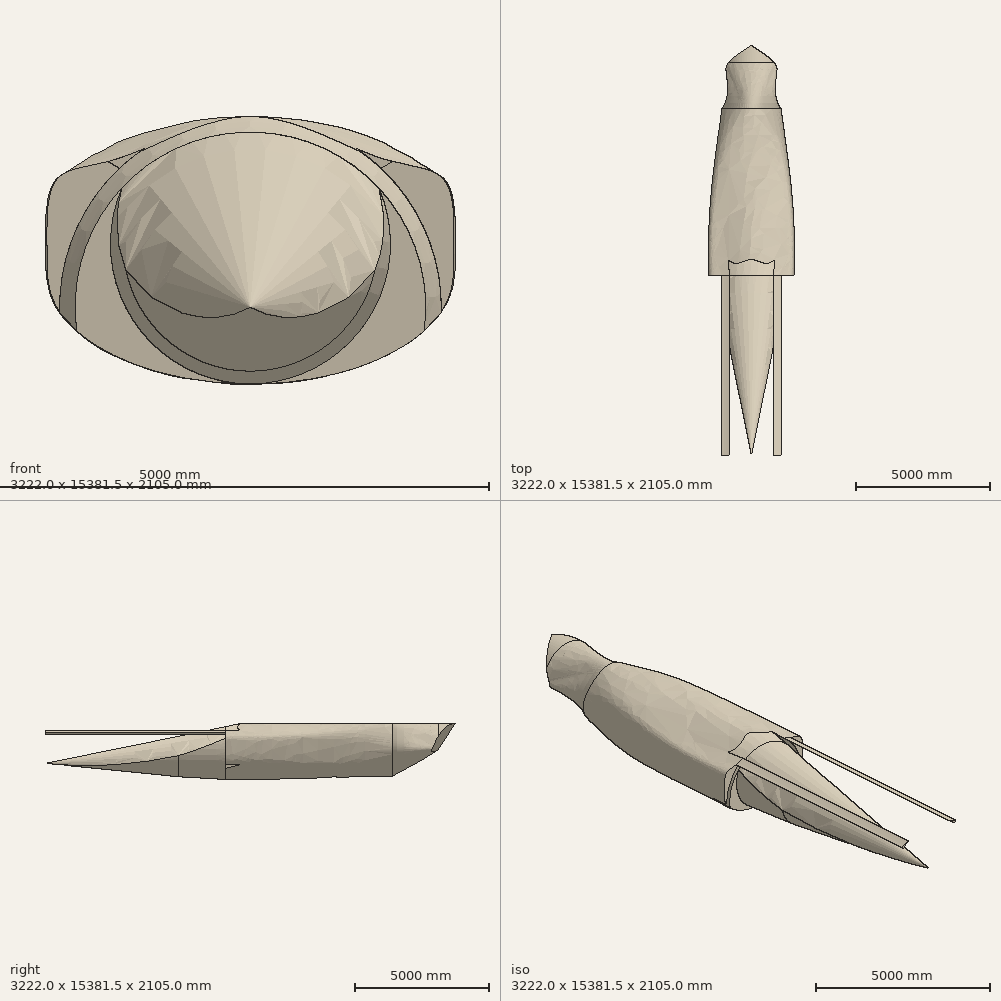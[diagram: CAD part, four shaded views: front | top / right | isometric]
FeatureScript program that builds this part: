
annotation { "Feature Type Name" : "Feature", "Feature Type Description" : "" }
export const myFeature = defineFeature(function(context is Context, id is Id, definition is map)
    precondition{}
    {
        {
            var Q0;
            Q0=qCreatedBy(makeId("Front.planeOp"),FACE);
            cPlane(context, id + "F0", {"entities" : qUnion([Q0]), "cplaneType" : CPlaneType.OFFSET, "offset" : 1750 * mm, "width" : 152.4 * mm, "height" : 152.4 * mm});
        }
        {
            var Q0;
            Q0=qCreatedBy(id+"F0.planeOp",FACE);
            var sketch = newSketch(context, id + "F1", { "sketchPlane" : qUnion([Q0])});
            skPoint(sketch, "E0.middle", {"position": v(0, 0) * mm});
            skFitSpline(sketch, "E1", {"points": [v(0, 1000) * mm, v(1060, 662.5) * mm, v(1517.6, 506.84) * mm, v(1600, 0) * mm, v(1517.6, -506.84) * mm, v(750, -1000) * mm, v(-750, -1000) * mm, v(-1517.6, -506.84) * mm, v(-1600, 0) * mm, v(-1517.6, 506.84) * mm, v(-1060, 662.5) * mm, v(0, 1000) * mm]});
            skSolve(sketch);
        }
        {
            var Q0;
            Q0=qCreatedBy(makeId("Front.planeOp"),FACE);
            var sketch = newSketch(context, id + "F2", { "sketchPlane" : qUnion([Q0])});
            skPoint(sketch, "E2.middle", {"position": v(0, 0) * mm});
            skFitSpline(sketch, "E3", {"points": [v(0, 1000) * mm, v(1060, 662.5) * mm, v(1517.6, 506.84) * mm, v(1600, 0) * mm, v(1517.6, -506.84) * mm, v(750, -1000) * mm, v(-750, -1000) * mm, v(-1517.6, -506.84) * mm, v(-1600, 0) * mm, v(-1517.6, 506.84) * mm, v(-1060, 662.5) * mm, v(0, 1000) * mm]});
            skSolve(sketch);
        }
        {
            var Q0;
            Q0=qCreatedBy(makeId("Front.planeOp"),FACE);
            cPlane(context, id + "F3", {"entities" : qUnion([Q0]), "cplaneType" : CPlaneType.OFFSET, "offset" : 3500 * mm, "oppositeDirection" : true, "width" : 150 * mm, "height" : 150 * mm});
        }
        {
            var Q0;
            Q0=qCreatedBy(id+"F3.planeOp",FACE);
            var sketch = newSketch(context, id + "F4", { "sketchPlane" : qUnion([Q0])});
            skPoint(sketch, "E4.middle", {"position": v(0, 0) * mm});
            skFitSpline(sketch, "E5", {"points": [v(0, 1000) * mm, v(1060, 662.5) * mm, v(1250, 0) * mm, v(1060, -662.5) * mm, v(0, -1000) * mm, v(-1060, -662.5) * mm, v(-1250, 0) * mm, v(-1060, 662.5) * mm, v(0, 1000) * mm]});
            skSolve(sketch);
        }
        {
            var Q0;
            Q0=qCreatedBy(makeId("Front.planeOp"),FACE);
            cPlane(context, id + "F5", {"entities" : qUnion([Q0]), "cplaneType" : CPlaneType.OFFSET, "offset" : 4500 * mm, "oppositeDirection" : true, "width" : 150 * mm, "height" : 150 * mm});
        }
        {
            var Q0;
            Q0=qCreatedBy(id+"F5.planeOp",FACE);
            var sketch = newSketch(context, id + "F6", { "sketchPlane" : qUnion([Q0])});
            skPoint(sketch, "E6.middle", {"position": v(0, 0) * mm});
            skFitSpline(sketch, "E7", {"points": [v(0, 1000) * mm, v(848, 530) * mm, v(1108.5, 0) * mm, v(848, -530) * mm, v(0, -1000) * mm, v(-848, -530) * mm, v(-1108.5, 0) * mm, v(-848, 530) * mm, v(0, 1000) * mm]});
            skSolve(sketch);
        }
        {
            var Q0;
            Q0=qCreatedBy(makeId("Front.planeOp"),FACE);
            cPlane(context, id + "F7", {"entities" : qUnion([Q0]), "cplaneType" : CPlaneType.OFFSET, "offset" : 6232.05 * mm, "oppositeDirection" : true, "width" : 150 * mm, "height" : 150 * mm});
        }
        {
            var Q0;
            Q0=qCreatedBy(id+"F7.planeOp",FACE);
            var sketch = newSketch(context, id + "F8", { "sketchPlane" : qUnion([Q0])});
            skArc(sketch, "E8", {"start": v(998.61, 52.63) * mm, "mid": v(0, 1000) * mm, "end": v(-998.61, 52.63) * mm});
            skLineSegment(sketch, "E9", {"start": v(0, 0) * mm, "end": v(-948.68, 0) * mm});
            skLineSegment(sketch, "E10", {"start": v(0, 0) * mm, "end": v(948.68, 0) * mm});
            skPoint(sketch, "E11.visualSharp", {"position": v(-1000, 0) * mm});
            skArc(sketch, "E11.filletArc", {"start": v(-998.61, 52.63) * mm, "mid": v(-984.96, 15.59) * mm, "end": v(-948.68, 0) * mm});
            skPoint(sketch, "E12.visualSharp", {"position": v(1000, 0) * mm});
            skArc(sketch, "E12.filletArc", {"start": v(948.68, 0) * mm, "mid": v(984.96, 15.59) * mm, "end": v(998.61, 52.63) * mm});
            skSolve(sketch);
        }
        {
            var Q0;
            Q0=sQuery(id+"F8.wireOp",EDGE,"E9");
            var Q1;
            Q1=sQuery(id+"F6.wireOp",VERTEX,"E7.6.internal");
            cPlane(context, id + "F9", {"entities" : qUnion([Q0, Q1]), "cplaneType" : CPlaneType.LINE_ANGLE, "offset" : 25 * mm, "angle" : 0 * degree, "width" : 150 * mm, "height" : 150 * mm});
        }
        {
            var Q0;
            Q0=qCreatedBy(id+"F9.planeOp",FACE);
            var sketch = newSketch(context, id + "F10", { "sketchPlane" : qUnion([Q0])});
            skFitSpline(sketch, "E13", {"points": [v(-1108.5, 4500) * mm, v(-948.68, 6232.05) * mm], "startDerivative": vector(1200, 1755) * mm, "endDerivative": vector(158.07, 1422.55) * mm});
            skFitSpline(sketch, "E14", {"points": [v(1108.5, 4500) * mm, v(948.68, 6232.05) * mm], "startDerivative": vector(-1200, 1755) * mm, "endDerivative": vector(-158.07, 1422.55) * mm});
            skSolve(sketch);
        }
        {
            var Q0;
            Q0=makeQuery(id+"F1.imprint","IMPRINT",FACE,{"disambiguationData":[TD([[makeQuery(id+"F1.imprint","IMPRINT",EDGE,{"derivedFrom":sQuery(id+"F1.wireOp",EDGE,"E1")}),-1.0]])]});
            var Q1;
            Q1=makeQuery(id+"F2.imprint","IMPRINT",FACE,{"disambiguationData":[TD([[makeQuery(id+"F2.imprint","IMPRINT",EDGE,{"derivedFrom":sQuery(id+"F2.wireOp",EDGE,"E3")}),-1.0]])]});
            var Q2;
            Q2=makeQuery(id+"F4.imprint","IMPRINT",FACE,{"disambiguationData":[TD([[makeQuery(id+"F4.imprint","IMPRINT",EDGE,{"derivedFrom":sQuery(id+"F4.wireOp",EDGE,"E5")}),-1.0]])]});
            var Q3;
            Q3=makeQuery(id+"F6.imprint","IMPRINT",FACE,{"disambiguationData":[TD([[makeQuery(id+"F6.imprint","IMPRINT",EDGE,{"derivedFrom":sQuery(id+"F6.wireOp",EDGE,"E7")}),-1.0]])]});
            loft(context, id + "F11", {"sheetProfilesArray" : [{ "sheetProfileEntities" : qUnion([Q0]) }, { "sheetProfileEntities" : qUnion([Q1]) }, { "sheetProfileEntities" : qUnion([Q2]) }, { "sheetProfileEntities" : qUnion([Q3]) }]});
        }
        {
            var Q1;
            Q1=makeQuery(id+"F6.imprint","IMPRINT",FACE,{"disambiguationData":[TD([[makeQuery(id+"F6.imprint","IMPRINT",EDGE,{"derivedFrom":sQuery(id+"F6.wireOp",EDGE,"E7")}),-1.0]])]});
            var Q2;
            Q2=makeQuery(id+"F8.imprint","IMPRINT",FACE,{"disambiguationData":[TD([[makeQuery(id+"F8.imprint","IMPRINT",EDGE,{"derivedFrom":sQuery(id+"F8.wireOp",EDGE,"E8")}),1.0]])]});
            var Q3;
            Q3=sQuery(id+"F10.wireOp",EDGE,"E13");
            var Q4;
            Q4=sQuery(id+"F10.wireOp",EDGE,"E14");
            loft(context, id + "F12", {"operationType" : NewBodyOperationType.ADD, "addGuides" : true, "sheetProfilesArray" : [{ "sheetProfileEntities" : qUnion([Q1]) }, { "sheetProfileEntities" : qUnion([Q2]) }], "guidesArray" : [{ "guideEntities" : qUnion([Q3]), "guideDerivativeType" : LoftGuideDerivativeType.DEFAULT, "guideDerivativeMagnitude" : 1 }, { "guideEntities" : qUnion([Q4]), "guideDerivativeType" : LoftGuideDerivativeType.DEFAULT, "guideDerivativeMagnitude" : 1 }]});
        }
        {
            var Q0;
            Q0 = qSketchRegion(id + "F1", true);
            extrude(context, id + "F13", {"entities" : qUnion([Q0]), "depth" : 6750 * mm});
        }
        {
            var Q0;
            Q0=qCreatedBy(makeId("Right.planeOp"),FACE);
            var sketch = newSketch(context, id + "F14", { "sketchPlane" : qUnion([Q0])});
            skLineSegment(sketch, "E15", {"start": v(0, 0) * mm, "end": v(-3500, 0) * mm});
            skLineSegment(sketch, "E16", {"start": v(-3500, 0) * mm, "end": v(-3500, -1000) * mm});
            skLineSegment(sketch, "E17", {"start": v(-3500, -1000) * mm, "end": v(-8500, -1000) * mm});
            skLineSegment(sketch, "E18", {"start": v(-8500, -1000) * mm, "end": v(-8500, -499.31) * mm});
            skLineSegment(sketch, "E19", {"start": v(-1151.4, 0) * mm, "end": v(-1151.4, 1000) * mm});
            skLineSegment(sketch, "E20", {"start": v(-1151.4, 1000) * mm, "end": v(-8500, -499.31) * mm});
            skLineSegment(sketch, "E21", {"start": v(-8500, -499.31) * mm, "end": v(-3500, -1000) * mm});
            skLineSegment(sketch, "E22", {"start": v(-3500, 1000) * mm, "end": v(4500, 1000) * mm});
            skLineSegment(sketch, "E23", {"start": v(-3500, 1000) * mm, "end": v(-8500, 1000) * mm});
            skLineSegment(sketch, "E24", {"start": v(-8500, 1000) * mm, "end": v(-8500, -499.31) * mm});
            skLineSegment(sketch, "E25", {"start": v(-8500, -1000) * mm, "end": v(-8500, -1750) * mm});
            skLineSegment(sketch, "E26", {"start": v(-8500, -1750) * mm, "end": v(-1750, -1750) * mm});
            skPoint(sketch, "E26.endSnap0", {"position": v(-1750, 0) * mm});
            skLineSegment(sketch, "E27", {"start": v(-1750, 0) * mm, "end": v(-1750, -1099.92) * mm});
            skLineSegment(sketch, "E28", {"start": v(-1750, -1099.92) * mm, "end": v(-3500, -1000) * mm});
            skLineSegment(sketch, "E29", {"start": v(-1750, -1099.92) * mm, "end": v(-1750, -1750) * mm});
            skLineSegment(sketch, "E30", {"start": v(-8500, -499.31) * mm, "end": v(-3500, -499.31) * mm});
            skSolve(sketch);
        }
        {
            var Q0;
            {var subQ0=sQuery(id+"F14.wireOp",EDGE,"E20");Q0=makeQuery(id+"F14.imprint","IMPRINT",FACE,{"disambiguationData":[TD([[makeQuery(id+"F14.imprint","IMPRINT",EDGE,{"derivedFrom":subQ0}),-1.0]])]});}
            var Q1;
            Q1=sQuery(id+"F14.wireOp",EDGE,"E30");
            revolve(context, id + "F15", {"operationType" : NewBodyOperationType.REMOVE, "entities" : qUnion([Q0]), "axis" : qUnion([Q1]), "revolveType" : RevolveType.SYMMETRIC, "oppositeDirection" : true, "angle" : 250 * degree});
        }
        {
            var Q0;
            Q0=makeQuery(id+"F14.imprint","IMPRINT",FACE,{"disambiguationData":[TD([[makeQuery(id+"F14.imprint","IMPRINT",EDGE,{"derivedFrom":sQuery(id+"F14.wireOp",EDGE,"E17")}),-1.0]])]});
            var Q1;
            Q1=makeQuery(id+"F14.imprint","IMPRINT",FACE,{"disambiguationData":[TD([[makeQuery(id+"F14.imprint","IMPRINT",EDGE,{"derivedFrom":sQuery(id+"F14.wireOp",EDGE,"E17")}),1.0]])]});
            var Q2;
            Q2=sQuery(id+"F14.wireOp",EDGE,"E15");
            revolve(context, id + "F16", {"operationType" : NewBodyOperationType.REMOVE, "entities" : qUnion([Q0, Q1]), "axis" : qUnion([Q2]), "revolveType" : RevolveType.SYMMETRIC, "oppositeDirection" : true, "angle" : 240 * degree});
        }
        {
            var Q0;
            Q0=makeQuery(id+"F12.opLoft","CAP_FACE",FACE,{"disambiguationData":[OSD([makeQuery(id+"F8.imprint","IMPRINT",FACE,{"disambiguationData":[TD([[makeQuery(id+"F8.imprint","IMPRINT",EDGE,{"derivedFrom":sQuery(id+"F8.wireOp",EDGE,"E8")}),1.0]])]})])],"isStart":true});
            extrude(context, id + "F17", {"entities" : qUnion([Q0]), "operationType" : NewBodyOperationType.ADD, "depth" : 649.4 * mm});
        }
        {
            var Q0;
            Q0=qCreatedBy(makeId("Right.planeOp"),FACE);
            var sketch = newSketch(context, id + "F18", { "sketchPlane" : qUnion([Q0])});
            skLineSegment(sketch, "E31", {"start": v(0, 0) * mm, "end": v(4500, 0) * mm});
            skLineSegment(sketch, "E32", {"start": v(4500, 0) * mm, "end": v(6232.05, 0) * mm});
            skLineSegment(sketch, "E33", {"start": v(4500, 0) * mm, "end": v(4500, 1000) * mm});
            skLineSegment(sketch, "E34", {"start": v(4500, 1000) * mm, "end": v(6881.46, 1000) * mm});
            skLineSegment(sketch, "E35", {"start": v(6881.46, 1000) * mm, "end": v(6881.46, -1000) * mm});
            skLineSegment(sketch, "E36", {"start": v(6881.46, 1000) * mm, "end": v(6232.05, 0) * mm});
            skLineSegment(sketch, "E37", {"start": v(6232.05, 0) * mm, "end": v(5582.64, -1000) * mm});
            skLineSegment(sketch, "E38", {"start": v(5582.64, -1000) * mm, "end": v(6881.46, -1000) * mm});
            skSolve(sketch);
        }
        {
            var Q0;
            Q0=makeQuery(id+"F18.imprint","IMPRINT",FACE,{"disambiguationData":[TD([[makeQuery(id+"F18.imprint","IMPRINT",EDGE,{"derivedFrom":sQuery(id+"F18.wireOp",EDGE,"E35")}),-1.0]])]});
            var Q1;
            Q1=sQuery(id+"F18.wireOp",EDGE,"E34");
            revolve(context, id + "F19", {"operationType" : NewBodyOperationType.REMOVE, "entities" : qUnion([Q0]), "axis" : qUnion([Q1]), "revolveType" : RevolveType.SYMMETRIC, "oppositeDirection" : true, "angle" : 182 * degree});
        }
    });
